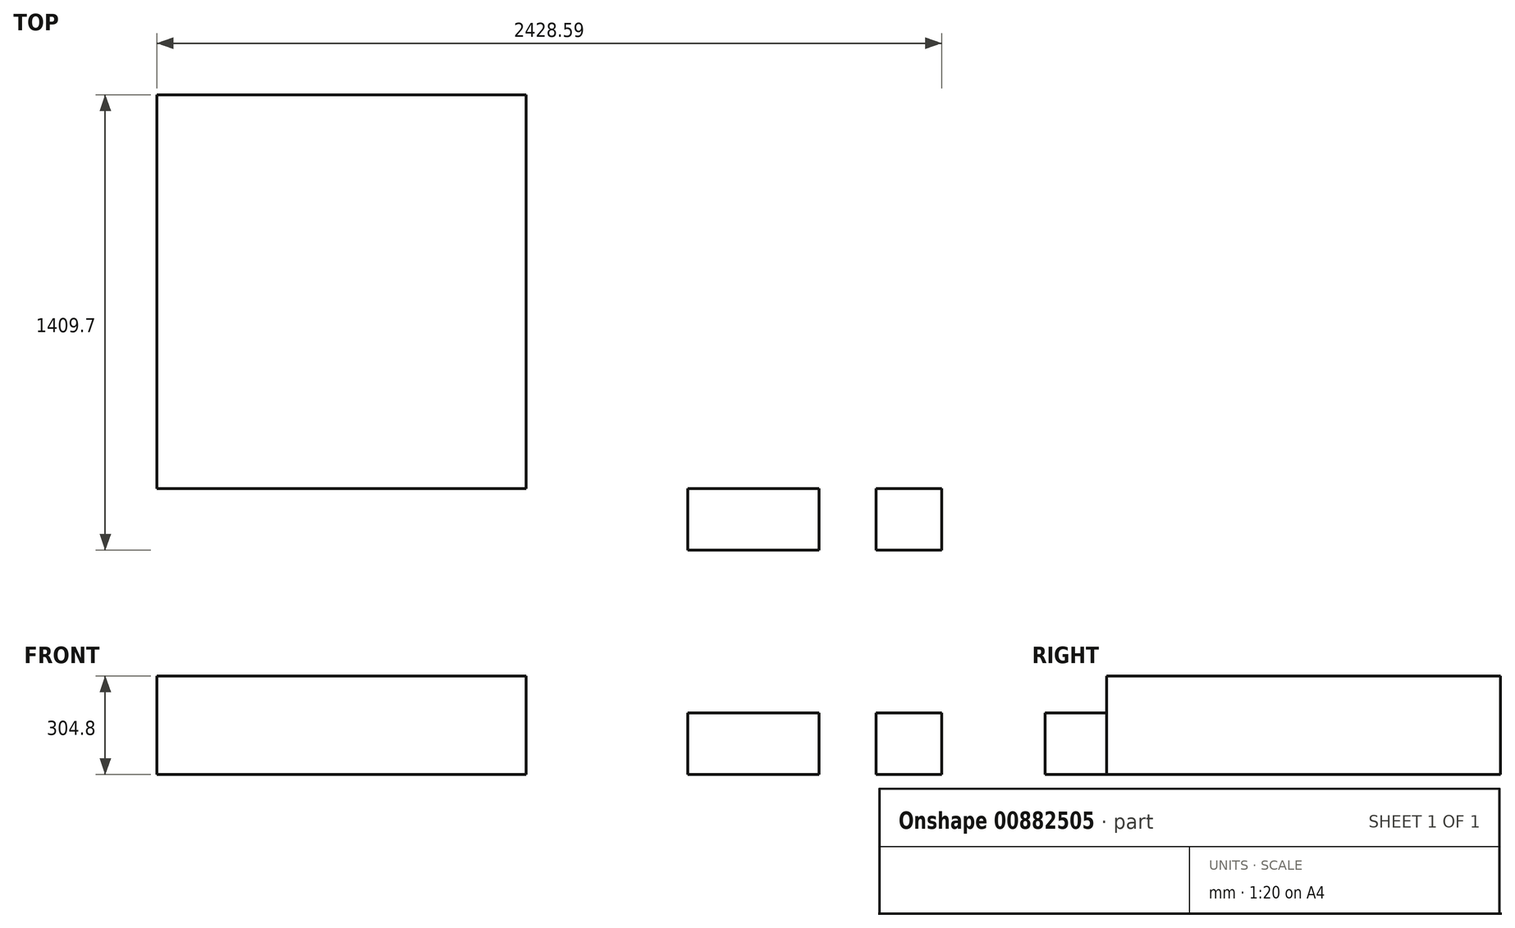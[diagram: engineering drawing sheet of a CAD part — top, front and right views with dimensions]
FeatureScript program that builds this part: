
annotation { "Feature Type Name" : "Feature", "Feature Type Description" : "" }
export const myFeature = defineFeature(function(context is Context, id is Id, definition is map)
    precondition{}
    {
        {
            var Q0;
            Q0=qCreatedBy(makeId("Front.planeOp"),FACE);
            var sketch = newSketch(context, id + "F0", { "sketchPlane" : qUnion([Q0])});
            skLineSegment(sketch, "E0.bottom", {"start": v(0, 0) * mm, "end": v(406.4, 0) * mm});
            skLineSegment(sketch, "E0.top", {"start": v(0, 190.5) * mm, "end": v(406.4, 190.5) * mm});
            skLineSegment(sketch, "E0.left", {"start": v(0, 0) * mm, "end": v(0, 190.5) * mm});
            skLineSegment(sketch, "E0.right", {"start": v(406.4, 0) * mm, "end": v(406.4, 190.5) * mm});
            skSolve(sketch);
        }
        {
            var Q0;
            Q0=makeQuery(id+"F0.imprint","IMPRINT",FACE,{"disambiguationData":[TD([[makeQuery(id+"F0.imprint","IMPRINT",EDGE,{"derivedFrom":sQuery(id+"F0.wireOp",EDGE,"E0.bottom")}),1.0]])]});
            extrude(context, id + "F1", {"entities" : qUnion([Q0]), "depth" : 190.5 * mm, "offsetDistance" : 25 * mm});
        }
        {
            var Q0;
            Q0=qCreatedBy(makeId("Front.planeOp"),FACE);
            var sketch = newSketch(context, id + "F2", { "sketchPlane" : qUnion([Q0])});
            skLineSegment(sketch, "E1.bottom", {"start": v(582.96, 0) * mm, "end": v(786.16, 0) * mm});
            skLineSegment(sketch, "E1.top", {"start": v(582.96, 190.5) * mm, "end": v(786.16, 190.5) * mm});
            skLineSegment(sketch, "E1.left", {"start": v(582.96, 0) * mm, "end": v(582.96, 190.5) * mm});
            skLineSegment(sketch, "E1.right", {"start": v(786.16, 0) * mm, "end": v(786.16, 190.5) * mm});
            skSolve(sketch);
        }
        {
            var Q0;
            Q0=makeQuery(id+"F2.imprint","IMPRINT",FACE,{"disambiguationData":[TD([[makeQuery(id+"F2.imprint","IMPRINT",EDGE,{"derivedFrom":sQuery(id+"F2.wireOp",EDGE,"E1.bottom")}),1.0]])]});
            extrude(context, id + "F3", {"entities" : qUnion([Q0]), "depth" : 190.5 * mm, "offsetDistance" : 25 * mm});
        }
        {
            var Q0;
            Q0=qCreatedBy(makeId("Top.planeOp"),FACE);
            var sketch = newSketch(context, id + "F4", { "sketchPlane" : qUnion([Q0])});
            skLineSegment(sketch, "E2.bottom", {"start": v(-1642.43, 0) * mm, "end": v(-499.43, 0) * mm});
            skLineSegment(sketch, "E2.top", {"start": v(-1642.43, 1219.2) * mm, "end": v(-499.43, 1219.2) * mm});
            skLineSegment(sketch, "E2.left", {"start": v(-1642.43, 0) * mm, "end": v(-1642.43, 1219.2) * mm});
            skLineSegment(sketch, "E2.right", {"start": v(-499.43, 0) * mm, "end": v(-499.43, 1219.2) * mm});
            skSolve(sketch);
        }
        {
            var Q0;
            Q0=makeQuery(id+"F4.imprint","IMPRINT",FACE,{"disambiguationData":[TD([[makeQuery(id+"F4.imprint","IMPRINT",EDGE,{"derivedFrom":sQuery(id+"F4.wireOp",EDGE,"E2.bottom")}),1.0]])]});
            extrude(context, id + "F5", {"entities" : qUnion([Q0]), "depth" : 304.8 * mm, "offsetDistance" : 25 * mm});
        }
    });
